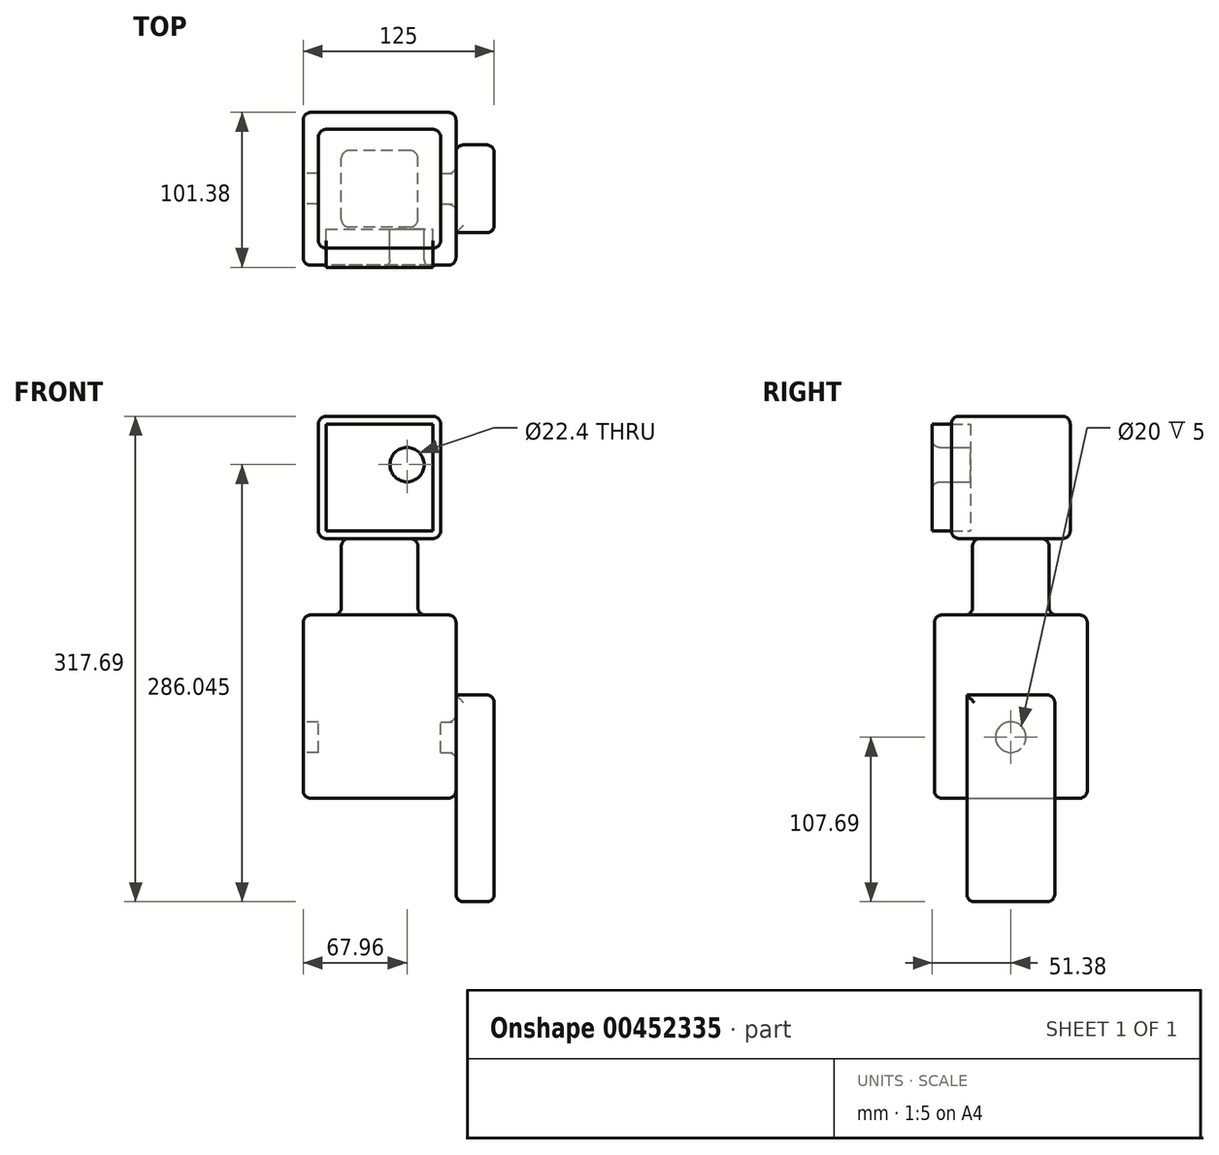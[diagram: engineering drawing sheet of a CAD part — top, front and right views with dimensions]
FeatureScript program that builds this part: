
annotation { "Feature Type Name" : "Feature", "Feature Type Description" : "" }
export const myFeature = defineFeature(function(context is Context, id is Id, definition is map)
    precondition{}
    {
        {
            var Q0;
            Q0=qCreatedBy(makeId("Top.planeOp"),FACE);
            var sketch = newSketch(context, id + "F0", { "sketchPlane" : qUnion([Q0])});
            skLineSegment(sketch, "E0.bottom", {"start": v(50, -50) * mm, "end": v(-50, -50) * mm});
            skLineSegment(sketch, "E0.top", {"start": v(50, 50) * mm, "end": v(-50, 50) * mm});
            skLineSegment(sketch, "E0.left", {"start": v(50, -50) * mm, "end": v(50, 50) * mm});
            skLineSegment(sketch, "E0.right", {"start": v(-50, -50) * mm, "end": v(-50, 50) * mm});
            skPoint(sketch, "E0.middle", {"position": v(0, 0) * mm});
            skSolve(sketch);
        }
        {
            var Q0;
            Q0=makeQuery(id+"F0.imprint","IMPRINT",FACE,{"disambiguationData":[TD([[makeQuery(id+"F0.imprint","IMPRINT",EDGE,{"derivedFrom":sQuery(id+"F0.wireOp",EDGE,"E0.bottom")}),-1.0]])]});
            extrude(context, id + "F1", {"entities" : qUnion([Q0]), "depth" : 120 * mm});
        }
        {
            var Q0;
            Q0=qCreatedBy(makeId("Top.planeOp"),FACE);
            cPlane(context, id + "F2", {"entities" : qUnion([Q0]), "cplaneType" : CPlaneType.OFFSET, "offset" : 120 * mm, "width" : 150 * mm, "height" : 150 * mm});
        }
        {
            var Q0;
            Q0=qCreatedBy(id+"F2.planeOp",FACE);
            var sketch = newSketch(context, id + "F3", { "sketchPlane" : qUnion([Q0])});
            skLineSegment(sketch, "E1.bottom", {"start": v(25, -25) * mm, "end": v(-25, -25) * mm});
            skLineSegment(sketch, "E1.top", {"start": v(25, 25) * mm, "end": v(-25, 25) * mm});
            skLineSegment(sketch, "E1.left", {"start": v(25, -25) * mm, "end": v(25, 25) * mm});
            skLineSegment(sketch, "E1.right", {"start": v(-25, -25) * mm, "end": v(-25, 25) * mm});
            skPoint(sketch, "E1.middle", {"position": v(0, 0) * mm});
            skSolve(sketch);
        }
        {
            var Q0;
            Q0=makeQuery(id+"F3.imprint","IMPRINT",FACE,{"disambiguationData":[TD([[makeQuery(id+"F3.imprint","IMPRINT",EDGE,{"derivedFrom":sQuery(id+"F3.wireOp",EDGE,"E1.bottom")}),-1.0]])]});
            extrude(context, id + "F4", {"entities" : qUnion([Q0]), "operationType" : NewBodyOperationType.ADD, "depth" : 50 * mm});
        }
        {
            var Q0;
            Q0=qCreatedBy(id+"F2.planeOp",FACE);
            cPlane(context, id + "F5", {"entities" : qUnion([Q0]), "cplaneType" : CPlaneType.OFFSET, "offset" : 50 * mm, "width" : 150 * mm, "height" : 150 * mm});
        }
        {
            var Q0;
            Q0=qCreatedBy(id+"F5.planeOp",FACE);
            var sketch = newSketch(context, id + "F6", { "sketchPlane" : qUnion([Q0])});
            skLineSegment(sketch, "E2.bottom", {"start": v(-40, -38.88) * mm, "end": v(40, -38.88) * mm});
            skLineSegment(sketch, "E2.top", {"start": v(-40, 38.88) * mm, "end": v(40, 38.88) * mm});
            skLineSegment(sketch, "E2.left", {"start": v(-40, -38.88) * mm, "end": v(-40, 38.88) * mm});
            skLineSegment(sketch, "E2.right", {"start": v(40, -38.88) * mm, "end": v(40, 38.88) * mm});
            skPoint(sketch, "E2.middle", {"position": v(0, 0) * mm});
            skSolve(sketch);
        }
        {
            var Q0;
            Q0 = qSketchRegion(id + "F6", true);
            extrude(context, id + "F7", {"entities" : qUnion([Q0]), "depth" : 80 * mm});
        }
        {
            var Q0;
            Q0=qCreatedBy(makeId("Right.planeOp"),FACE);
            cPlane(context, id + "F8", {"entities" : qUnion([Q0]), "cplaneType" : CPlaneType.OFFSET, "offset" : 50 * mm, "width" : 150 * mm, "height" : 150 * mm});
        }
        {
            var Q0;
            Q0=qCreatedBy(id+"F8.planeOp",FACE);
            var sketch = newSketch(context, id + "F9", { "sketchPlane" : qUnion([Q0])});
            skLineSegment(sketch, "E3", {"start": v(0, 0) * mm, "end": v(0, 40) * mm});
            skCircle(sketch, "E4", {"center": v(0, 40) * mm, "radius": 10 * mm});
            skSolve(sketch);
        }
        {
            var Q0;
            Q0=makeQuery(id+"F9.imprint","IMPRINT",FACE,{"disambiguationData":[TD([[makeQuery(id+"F9.imprint","IMPRINT",EDGE,{"derivedFrom":sQuery(id+"F9.wireOp",EDGE,"E4")}),1.0]])]});
            extrude(context, id + "F10", {"entities" : qUnion([Q0]), "oppositeDirection" : true, "depth" : 10 * mm});
        }
        {
            var Q0;
            Q0=makeQuery(id+"F1.opExtrude","SWEPT_FACE",FACE,{"disambiguationData":[OSD([sQuery(id+"F0.wireOp",EDGE,"E0.left")])]});
            var sketch = newSketch(context, id + "F11", { "sketchPlane" : qUnion([Q0])});
            skLineSegment(sketch, "E5.bottom", {"start": v(28.75, 67.69) * mm, "end": v(-28.75, 67.69) * mm});
            skLineSegment(sketch, "E5.top", {"start": v(28.75, -67.69) * mm, "end": v(-28.75, -67.69) * mm});
            skLineSegment(sketch, "E5.left", {"start": v(28.75, 67.69) * mm, "end": v(28.75, -67.69) * mm});
            skLineSegment(sketch, "E5.right", {"start": v(-28.75, 67.69) * mm, "end": v(-28.75, -67.69) * mm});
            skPoint(sketch, "E5.middle", {"position": v(0, 0) * mm});
            skSolve(sketch);
        }
        {
            var Q0;
            {var subQ0=sQuery(id+"F11.wireOp",EDGE,"E5.top");Q0=makeQuery(id+"F11.imprint","IMPRINT",FACE,{"disambiguationData":[TD([[makeQuery(id+"F11.imprint","IMPRINT",EDGE,{"derivedFrom":subQ0}),-1.0]])]});}
            var Q1;
            {var subQ0=sQuery(id+"F11.wireOp",EDGE,"E5.bottom");Q1=makeQuery(id+"F11.imprint","IMPRINT",FACE,{"disambiguationData":[TD([[makeQuery(id+"F11.imprint","IMPRINT",EDGE,{"derivedFrom":subQ0}),1.0]])]});}
            extrude(context, id + "F12", {"entities" : qUnion([Q0, Q1]), "depth" : 25 * mm});
        }
        {
            var Q0;
            Q0=makeQuery(id+"F10.opExtrude","SWEPT_BODY",BODY,{"disambiguationData":[OSD([sQuery(id+"F9.wireOp",EDGE,"E4")])]});
            var Q1;
            Q1=makeQuery(id+"F1.opExtrude","SWEPT_BODY",BODY,{"disambiguationData":[OSD([sQuery(id+"F0.wireOp",EDGE,"E0.bottom"),sQuery(id+"F0.wireOp",EDGE,"E0.top"),sQuery(id+"F0.wireOp",EDGE,"E0.left"),sQuery(id+"F0.wireOp",EDGE,"E0.right")])]});
            booleanBodies(context, id + "F13", {"operationType" : BooleanOperationType.SUBTRACTION, "tools" : qUnion([Q0]), "targets" : qUnion([Q1]), "keepTools" : true});
        }
        {
            var Q0;
            Q0=makeQuery(id+"F10.opExtrude","SWEPT_BODY",BODY,{"disambiguationData":[OSD([sQuery(id+"F9.wireOp",EDGE,"E4")])]});
            var Q1;
            Q1=qCreatedBy(makeId("Right.planeOp"),FACE);
            mirror(context, id + "F14", {"entities" : qUnion([Q0]), "mirrorPlane" : qUnion([Q1])});
        }
        {
            var Q0;
            Q0=makeQuery(id+"F1.opExtrude","SWEPT_FACE",FACE,{"disambiguationData":[OSD([sQuery(id+"F0.wireOp",EDGE,"E0.bottom")])]});
            var Q1;
            Q1=makeQuery(id+"F1.opExtrude","SWEPT_FACE",FACE,{"disambiguationData":[OSD([sQuery(id+"F0.wireOp",EDGE,"E0.right")])]});
            var Q2;
            Q2=makeQuery(id+"F1.opExtrude","CAP_FACE",FACE,{"disambiguationData":[OSD([sQuery(id+"F0.wireOp",EDGE,"E0.bottom"),sQuery(id+"F0.wireOp",EDGE,"E0.top"),sQuery(id+"F0.wireOp",EDGE,"E0.left"),sQuery(id+"F0.wireOp",EDGE,"E0.right")])],"isStart":false});
            var Q3;
            Q3=makeQuery(id+"F4.opExtrude","SWEPT_FACE",FACE,{"disambiguationData":[OSD([sQuery(id+"F3.wireOp",EDGE,"E1.bottom")])]});
            var Q4;
            Q4=makeQuery(id+"F4.opExtrude","SWEPT_EDGE",EDGE,{"disambiguationData":[OSD([sQuery(id+"F3.wireOp",EDGE,"E1.top"),sQuery(id+"F3.wireOp",EDGE,"E1.right")])]});
            var Q5;
            Q5=makeQuery(id+"F7.opExtrude","SWEPT_FACE",FACE,{"disambiguationData":[OSD([sQuery(id+"F6.wireOp",EDGE,"E2.bottom")])]});
            var Q6;
            Q6=makeQuery(id+"F7.opExtrude","SWEPT_FACE",FACE,{"disambiguationData":[OSD([sQuery(id+"F6.wireOp",EDGE,"E2.left")])]});
            var Q7;
            Q7=makeQuery(id+"F12.opExtrude","CAP_FACE",FACE,{"disambiguationData":[OSD([sQuery(id+"F11.wireOp",EDGE,"E5.bottom"),sQuery(id+"F11.wireOp",EDGE,"E5.top"),sQuery(id+"F11.wireOp",EDGE,"E5.left"),sQuery(id+"F11.wireOp",EDGE,"E5.right")])],"isStart":false});
            var Q8;
            Q8=makeQuery(id+"F1.opExtrude","SWEPT_FACE",FACE,{"disambiguationData":[OSD([sQuery(id+"F0.wireOp",EDGE,"E0.left")])]});
            var Q9;
            Q9=makeQuery(id+"F7.opExtrude","SWEPT_FACE",FACE,{"disambiguationData":[OSD([sQuery(id+"F6.wireOp",EDGE,"E2.top")])]});
            var Q10;
            Q10=makeQuery(id+"F7.opExtrude","SWEPT_FACE",FACE,{"disambiguationData":[OSD([sQuery(id+"F6.wireOp",EDGE,"E2.right")])]});
            var Q11;
            Q11=makeQuery(id+"F4.opExtrude","SWEPT_FACE",FACE,{"disambiguationData":[OSD([sQuery(id+"F3.wireOp",EDGE,"E1.left")])]});
            var Q12;
            Q12=makeQuery(id+"F4.opExtrude","SWEPT_FACE",FACE,{"disambiguationData":[OSD([sQuery(id+"F3.wireOp",EDGE,"E1.top")])]});
            var Q13;
            Q13=makeQuery(id+"F1.opExtrude","SWEPT_FACE",FACE,{"disambiguationData":[OSD([sQuery(id+"F0.wireOp",EDGE,"E0.top")])]});
            var Q14;
            Q14=makeQuery(id+"F14.opPattern","COPY",FACE,{"derivedFrom":makeQuery(id+"F12.opExtrude","CAP_FACE",FACE,{"disambiguationData":[OSD([sQuery(id+"F11.wireOp",EDGE,"E5.bottom"),sQuery(id+"F11.wireOp",EDGE,"E5.top"),sQuery(id+"F11.wireOp",EDGE,"E5.left"),sQuery(id+"F11.wireOp",EDGE,"E5.right")])],"isStart":true}),"instanceName":"1"});
            var Q15;
            Q15=makeQuery(id+"F14.opPattern","COPY",EDGE,{"derivedFrom":makeQuery(id+"F12.opExtrude","CAP_EDGE",EDGE,{"disambiguationData":[OSD([sQuery(id+"F11.wireOp",EDGE,"E5.left")])],"isStart":false}),"instanceName":"1"});
            var Q16;
            Q16=makeQuery(id+"F12.opExtrude","SWEPT_FACE",FACE,{"disambiguationData":[OSD([sQuery(id+"F11.wireOp",EDGE,"E5.left")])]});
            fillet(context, id + "F15", {"entities" : qUnion([Q0, Q1, Q2, Q3, Q4, Q5, Q6, Q7, Q8, Q9, Q10, Q11, Q12, Q13, Q14, Q15, Q16]), "radius" : 5 * mm, "tangentPropagation" : true, "allowEdgeOverflow" : false});
        }
        {
            var Q0;
            Q0=makeQuery(id+"F7.opExtrude","SWEPT_FACE",FACE,{"disambiguationData":[OSD([sQuery(id+"F6.wireOp",EDGE,"E2.bottom")])]});
            var sketch = newSketch(context, id + "F16", { "sketchPlane" : qUnion([Q0])});
            skCircle(sketch, "E6", {"center": v(-17.96, 218.36) * mm, "radius": 11.2 * mm});
            skCircle(sketch, "E7.MirrorC", {"center": v(17.96, 218.36) * mm, "radius": 11.2 * mm});
            skSolve(sketch);
        }
        {
            var Q0;
            Q0=makeQuery(id+"F16.imprint","IMPRINT",FACE,{"disambiguationData":[TD([[makeQuery(id+"F16.imprint","IMPRINT",EDGE,{"derivedFrom":sQuery(id+"F16.wireOp",EDGE,"E6")}),1.0]])]});
            var Q1;
            Q1=makeQuery(id+"F16.imprint","IMPRINT",FACE,{"disambiguationData":[TD([[makeQuery(id+"F16.imprint","IMPRINT",EDGE,{"derivedFrom":sQuery(id+"F16.wireOp",EDGE,"E7.MirrorC")}),-1.0]])]});
            extrude(context, id + "F17", {"entities" : qUnion([Q0, Q1]), "endBound" : BoundingType.SYMMETRIC, "depth" : 25 * mm});
        }
        {
            var Q0;
            Q0=makeQuery(id+"F17.opExtrude","SWEPT_BODY",BODY,{"disambiguationData":[OSD([sQuery(id+"F16.wireOp",EDGE,"E6")])]});
            var Q1;
            Q1=makeQuery(id+"F17.opExtrude","SWEPT_BODY",BODY,{"disambiguationData":[OSD([sQuery(id+"F16.wireOp",EDGE,"E7.MirrorC")])]});
            var Q2;
            Q2=makeQuery(id+"F7.opExtrude","SWEPT_BODY",BODY,{"disambiguationData":[OSD([sQuery(id+"F6.wireOp",EDGE,"E2.bottom"),sQuery(id+"F6.wireOp",EDGE,"E2.top"),sQuery(id+"F6.wireOp",EDGE,"E2.left"),sQuery(id+"F6.wireOp",EDGE,"E2.right")])]});
            booleanBodies(context, id + "F18", {"operationType" : BooleanOperationType.SUBTRACTION, "tools" : qUnion([Q0, Q1]), "targets" : qUnion([Q2]), "keepTools" : true});
        }
        {
            var Q0;
            Q0=makeQuery(id+"F17.opExtrude","CAP_EDGE",EDGE,{"disambiguationData":[OSD([sQuery(id+"F16.wireOp",EDGE,"E6")])],"isStart":false});
            var Q1;
            Q1=makeQuery(id+"F17.opExtrude","CAP_EDGE",EDGE,{"disambiguationData":[OSD([sQuery(id+"F16.wireOp",EDGE,"E7.MirrorC")])],"isStart":false});
            fillet(context, id + "F19", {"entities" : qUnion([Q0, Q1]), "radius" : 5 * mm, "tangentPropagation" : true, "allowEdgeOverflow" : false});
        }
        {
            var Q0;
            Q0=makeQuery(id+"F4.opExtrude","SWEPT_FACE",FACE,{"disambiguationData":[OSD([sQuery(id+"F3.wireOp",EDGE,"E1.right")])]});
            fillet(context, id + "F20", {"entities" : qUnion([Q0]), "radius" : 5 * mm, "tangentPropagation" : true, "allowEdgeOverflow" : false});
        }
        {
            var Q0;
            Q0=makeQuery(id+"F14.opPattern","COPY",FACE,{"derivedFrom":makeQuery(id+"F12.opExtrude","CAP_FACE",FACE,{"disambiguationData":[OSD([sQuery(id+"F11.wireOp",EDGE,"E5.bottom"),sQuery(id+"F11.wireOp",EDGE,"E5.top"),sQuery(id+"F11.wireOp",EDGE,"E5.left"),sQuery(id+"F11.wireOp",EDGE,"E5.right")])],"isStart":false}),"instanceName":"1"});
            var Q1;
            Q1=makeQuery(id+"F14.opPattern","COPY",FACE,{"derivedFrom":makeQuery(id+"F12.opExtrude","SWEPT_FACE",FACE,{"disambiguationData":[OSD([sQuery(id+"F11.wireOp",EDGE,"E5.top")])]}),"instanceName":"1"});
            var Q2;
            Q2=makeQuery(id+"F12.opExtrude","SWEPT_FACE",FACE,{"disambiguationData":[OSD([sQuery(id+"F11.wireOp",EDGE,"E5.top")])]});
            fillet(context, id + "F21", {"entities" : qUnion([Q0, Q1, Q2]), "radius" : 5 * mm, "tangentPropagation" : true, "allowEdgeOverflow" : false});
        }
    });
